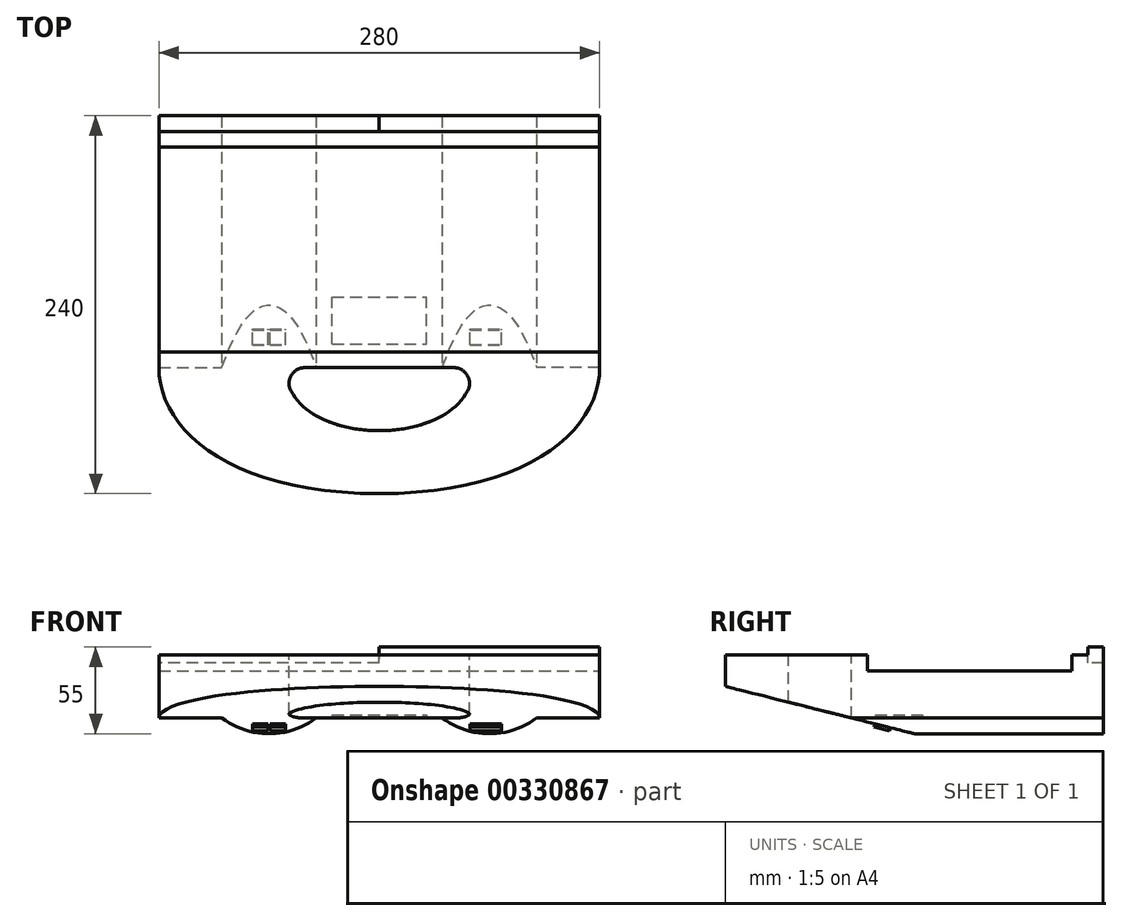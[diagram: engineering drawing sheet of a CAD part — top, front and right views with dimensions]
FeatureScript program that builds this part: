
annotation { "Feature Type Name" : "Feature", "Feature Type Description" : "" }
export const myFeature = defineFeature(function(context is Context, id is Id, definition is map)
    precondition{}
    {
        {
            var Q0;
            Q0=qCreatedBy(makeId("Front.planeOp"),FACE);
            var sketch = newSketch(context, id + "F0", { "sketchPlane" : qUnion([Q0])});
            skLineSegment(sketch, "E0", {"start": v(0, 34.56) * mm, "end": v(-140, 34.56) * mm});
            skLineSegment(sketch, "E1", {"start": v(-140, 34.56) * mm, "end": v(-140, -15.44) * mm});
            skLineSegment(sketch, "E2", {"start": v(-140, -15.44) * mm, "end": v(0, -15.44) * mm});
            skLineSegment(sketch, "E3.MirrorCS", {"start": v(0, 34.56) * mm, "end": v(140, 34.56) * mm});
            skLineSegment(sketch, "E4.MirrorCS", {"start": v(140, 34.56) * mm, "end": v(140, -15.44) * mm});
            skLineSegment(sketch, "E5.MirrorCS", {"start": v(140, -15.44) * mm, "end": v(0, -15.44) * mm});
            skSolve(sketch);
        }
        {
            var Q0;
            Q0 = qSketchRegion(id + "F0", true);
            extrude(context, id + "F1", {"entities" : qUnion([Q0]), "depth" : 240 * mm});
        }
        {
            var Q0;
            Q0=makeQuery(id+"F1.opExtrude","SWEPT_FACE",FACE,{"disambiguationData":[OSD([sQuery(id+"F0.wireOp",EDGE,"E0"),sQuery(id+"F0.wireOp",EDGE,"E3.MirrorCS")])]});
            var sketch = newSketch(context, id + "F2", { "sketchPlane" : qUnion([Q0])});
            skFitSpline(sketch, "E6", {"points": [v(0, -240) * mm, v(-140, -160) * mm], "startDerivative": vector(-286.06, 0) * mm, "endDerivative": vector(0, 116.3) * mm});
            skLineSegment(sketch, "E7", {"start": v(-140, -160) * mm, "end": v(-197.98, -160) * mm});
            skLineSegment(sketch, "E8", {"start": v(-197.98, -160) * mm, "end": v(-197.98, -279.95) * mm});
            skLineSegment(sketch, "E9", {"start": v(-197.98, -279.95) * mm, "end": v(0, -279.95) * mm});
            skLineSegment(sketch, "E10.MirrorCS", {"start": v(197.98, -279.95) * mm, "end": v(0, -279.95) * mm});
            skLineSegment(sketch, "E11.MirrorCS", {"start": v(197.98, -160) * mm, "end": v(197.98, -279.95) * mm});
            skLineSegment(sketch, "E12.MirrorCS", {"start": v(140, -160) * mm, "end": v(197.98, -160) * mm});
            skFitSpline(sketch, "E13.MirrorCS", {"points": [v(0, -240) * mm, v(140, -160) * mm], "startDerivative": vector(286.06, 0) * mm, "endDerivative": vector(0, 116.3) * mm});
            skSolve(sketch);
        }
        {
            var Q0;
            Q0=makeQuery(id+"F1.opExtrude","SWEPT_FACE",FACE,{"disambiguationData":[OSD([sQuery(id+"F0.wireOp",EDGE,"E4.MirrorCS")])]});
            var sketch = newSketch(context, id + "F3", { "sketchPlane" : qUnion([Q0])});
            skLineSegment(sketch, "E14", {"start": v(-240, 14.56) * mm, "end": v(-258.73, 14.56) * mm});
            skLineSegment(sketch, "E15", {"start": v(-258.73, 14.56) * mm, "end": v(-258.73, -38.28) * mm});
            skLineSegment(sketch, "E16", {"start": v(-258.73, -38.28) * mm, "end": v(-129.87, -38.28) * mm});
            skLineSegment(sketch, "E17", {"start": v(-129.87, -38.28) * mm, "end": v(-120, -15.44) * mm});
            skLineSegment(sketch, "E18", {"start": v(-240, 14.56) * mm, "end": v(-160, -5.44) * mm});
            skLineSegment(sketch, "E19", {"start": v(-160, -5.44) * mm, "end": v(-120, -15.44) * mm});
            skSolve(sketch);
        }
        {
            var Q0;
            Q0=makeQuery(id+"F1.opExtrude","CAP_FACE",FACE,{"disambiguationData":[OSD([sQuery(id+"F0.wireOp",EDGE,"E0"),sQuery(id+"F0.wireOp",EDGE,"E1"),sQuery(id+"F0.wireOp",EDGE,"E2"),sQuery(id+"F0.wireOp",EDGE,"E3.MirrorCS"),sQuery(id+"F0.wireOp",EDGE,"E4.MirrorCS"),sQuery(id+"F0.wireOp",EDGE,"E5.MirrorCS")])],"isStart":false});
            var sketch = newSketch(context, id + "F4", { "sketchPlane" : qUnion([Q0])});
            skLineSegment(sketch, "E20", {"start": v(-140, -5.44) * mm, "end": v(-165.94, -5.44) * mm});
            skLineSegment(sketch, "E21", {"start": v(-165.94, -5.44) * mm, "end": v(-165.94, -57.66) * mm});
            skLineSegment(sketch, "E22", {"start": v(-165.94, -57.66) * mm, "end": v(0, -57.66) * mm});
            skLineSegment(sketch, "E23", {"start": v(-140, -5.44) * mm, "end": v(-100, -5.44) * mm});
            skLineSegment(sketch, "E24", {"start": v(0, -5.44) * mm, "end": v(-40, -5.44) * mm});
            skArc(sketch, "E25", {"start": v(-70, -15.44) * mm, "mid": v(-85.81, -12.88) * mm, "end": v(-100, -5.44) * mm});
            skArc(sketch, "E26", {"start": v(-70, -15.44) * mm, "mid": v(-54.19, -12.88) * mm, "end": v(-40, -5.44) * mm});
            skLineSegment(sketch, "E27.MirrorCS", {"start": v(140, -5.44) * mm, "end": v(100, -5.44) * mm});
            skLineSegment(sketch, "E28.MirrorCS", {"start": v(140, -5.44) * mm, "end": v(165.94, -5.44) * mm});
            skLineSegment(sketch, "E29.MirrorCS", {"start": v(0, -5.44) * mm, "end": v(40, -5.44) * mm});
            skArc(sketch, "E30.MirrorCS", {"start": v(70, -15.44) * mm, "mid": v(85.81, -12.88) * mm, "end": v(100, -5.44) * mm});
            skLineSegment(sketch, "E31.MirrorCS", {"start": v(165.94, -57.66) * mm, "end": v(0, -57.66) * mm});
            skArc(sketch, "E32.MirrorCS", {"start": v(70, -15.44) * mm, "mid": v(54.19, -12.88) * mm, "end": v(40, -5.44) * mm});
            skLineSegment(sketch, "E33.MirrorCS", {"start": v(165.94, -5.44) * mm, "end": v(165.94, -57.66) * mm});
            skSolve(sketch);
        }
        {
            var Q0;
            Q0 = qSketchRegion(id + "F2", true);
            extrude(context, id + "F5", {"entities" : qUnion([Q0]), "operationType" : NewBodyOperationType.REMOVE, "oppositeDirection" : true, "depth" : 55 * mm});
        }
        {
            var Q0;
            Q0 = qSketchRegion(id + "F3", true);
            extrude(context, id + "F6", {"entities" : qUnion([Q0]), "operationType" : NewBodyOperationType.REMOVE, "oppositeDirection" : true, "depth" : 300 * mm});
        }
        {
            var Q0;
            Q0 = qSketchRegion(id + "F4", true);
            extrude(context, id + "F7", {"entities" : qUnion([Q0]), "operationType" : NewBodyOperationType.REMOVE, "oppositeDirection" : true, "depth" : 300 * mm});
        }
        {
            var Q0;
            Q0=makeQuery(id+"F1.opExtrude","SWEPT_FACE",FACE,{"disambiguationData":[OSD([sQuery(id+"F0.wireOp",EDGE,"E0"),sQuery(id+"F0.wireOp",EDGE,"E3.MirrorCS")])]});
            var sketch = newSketch(context, id + "F8", { "sketchPlane" : qUnion([Q0])});
            skLineSegment(sketch, "E34", {"start": v(-47.32, -160) * mm, "end": v(0, -160) * mm});
            skFitSpline(sketch, "E35", {"points": [v(-60, -160) * mm, v(0, -200.02) * mm], "startDerivative": vector(2.66, -80.66) * mm, "endDerivative": vector(88.67, 0) * mm});
            skFitSpline(sketch, "E36.MirrorCS", {"points": [v(60, -160) * mm, v(0, -200.02) * mm], "startDerivative": vector(-2.66, -80.66) * mm, "endDerivative": vector(-88.67, 0) * mm});
            skLineSegment(sketch, "E37.MirrorCS", {"start": v(47.32, -160) * mm, "end": v(0, -160) * mm});
            skArc(sketch, "E38.filletArc", {"start": v(-47.32, -160) * mm, "mid": v(-55.9, -164.85) * mm, "end": v(-56.14, -174.7) * mm});
            skArc(sketch, "E39.filletArc", {"start": v(56.14, -174.7) * mm, "mid": v(55.9, -164.85) * mm, "end": v(47.32, -160) * mm});
            skSolve(sketch);
        }
        {
            var Q0;
            Q0 = qSketchRegion(id + "F8", true);
            extrude(context, id + "F9", {"entities" : qUnion([Q0]), "operationType" : NewBodyOperationType.REMOVE, "oppositeDirection" : true, "depth" : 60 * mm});
        }
        {
            var Q0;
            Q0=makeQuery(id+"F1.opExtrude","SWEPT_FACE",FACE,{"disambiguationData":[OSD([sQuery(id+"F0.wireOp",EDGE,"E4.MirrorCS")])]});
            var sketch = newSketch(context, id + "F10", { "sketchPlane" : qUnion([Q0])});
            skLineSegment(sketch, "E40", {"start": v(-150, 34.56) * mm, "end": v(-150, 24.56) * mm});
            skLineSegment(sketch, "E41", {"start": v(-150, 24.56) * mm, "end": v(-20, 24.56) * mm});
            skLineSegment(sketch, "E42", {"start": v(-20, 24.56) * mm, "end": v(-20, 34.56) * mm});
            skLineSegment(sketch, "E43", {"start": v(-20, 34.56) * mm, "end": v(-20, 61.04) * mm});
            skLineSegment(sketch, "E44", {"start": v(-20, 61.04) * mm, "end": v(-150, 61.04) * mm});
            skLineSegment(sketch, "E45", {"start": v(-150, 61.04) * mm, "end": v(-150, 34.56) * mm});
            skSolve(sketch);
        }
        {
            var Q0;
            Q0 = qSketchRegion(id + "F10", true);
            extrude(context, id + "F11", {"entities" : qUnion([Q0]), "operationType" : NewBodyOperationType.REMOVE, "oppositeDirection" : true, "depth" : 300 * mm});
        }
        {
            var Q0;
            Q0=makeQuery(id+"F1.opExtrude","SWEPT_FACE",FACE,{"disambiguationData":[OSD([sQuery(id+"F0.wireOp",EDGE,"E1")])]});
            var sketch = newSketch(context, id + "F12", { "sketchPlane" : qUnion([Q0])});
            skLineSegment(sketch, "E46", {"start": v(0, 34.56) * mm, "end": v(0, 24.56) * mm});
            skLineSegment(sketch, "E47", {"start": v(0, 24.56) * mm, "end": v(10, 24.56) * mm});
            skLineSegment(sketch, "E48", {"start": v(10, 24.56) * mm, "end": v(10, 34.56) * mm});
            skLineSegment(sketch, "E49", {"start": v(10, 34.56) * mm, "end": v(0, 34.56) * mm});
            skSolve(sketch);
        }
        {
            var Q0;
            Q0 = qSketchRegion(id + "F12", true);
            extrude(context, id + "F13", {"entities" : qUnion([Q0]), "operationType" : NewBodyOperationType.REMOVE, "oppositeDirection" : true, "depth" : 140 * mm});
        }
        {
            var Q0;
            Q0=makeQuery(id+"F1.opExtrude","SWEPT_FACE",FACE,{"disambiguationData":[OSD([sQuery(id+"F0.wireOp",EDGE,"E4.MirrorCS")])]});
            var sketch = newSketch(context, id + "F14", { "sketchPlane" : qUnion([Q0])});
            skLineSegment(sketch, "E50", {"start": v(0, 34.56) * mm, "end": v(0, 39.56) * mm});
            skLineSegment(sketch, "E51", {"start": v(0, 39.56) * mm, "end": v(-10, 39.56) * mm});
            skLineSegment(sketch, "E52", {"start": v(-10, 39.56) * mm, "end": v(-10, 34.56) * mm});
            skSolve(sketch);
        }
        {
            var Q0;
            {var subQ0=sQuery(id+"F14.wireOp",EDGE,"E50");Q0=makeQuery(id+"F14.imprint","IMPRINT",FACE,{"disambiguationData":[TD([[makeQuery(id+"F14.imprint","IMPRINT",EDGE,{"derivedFrom":subQ0}),1.0]])]});}
            extrude(context, id + "F15", {"entities" : qUnion([Q0]), "operationType" : NewBodyOperationType.ADD, "oppositeDirection" : true, "depth" : 140 * mm});
        }
        {
            var Q0;
            Q0=makeQuery(id+"F1.opExtrude","SWEPT_FACE",FACE,{"disambiguationData":[OSD([sQuery(id+"F0.wireOp",EDGE,"E1")])]});
            var sketch = newSketch(context, id + "F16", { "sketchPlane" : qUnion([Q0])});
            skLineSegment(sketch, "E53", {"start": v(0, 24.56) * mm, "end": v(0, 29.56) * mm});
            skLineSegment(sketch, "E54", {"start": v(0, 29.56) * mm, "end": v(10, 29.56) * mm});
            skLineSegment(sketch, "E55", {"start": v(10, 29.56) * mm, "end": v(10, 24.56) * mm});
            skSolve(sketch);
        }
        {
            var Q0;
            Q0=makeQuery(id+"F16.imprint","IMPRINT",FACE,{"disambiguationData":[TD([[makeQuery(id+"F16.imprint","IMPRINT",EDGE,{"derivedFrom":sQuery(id+"F16.wireOp",EDGE,"E53")}),-1.0]])]});
            extrude(context, id + "F17", {"entities" : qUnion([Q0]), "operationType" : NewBodyOperationType.ADD, "oppositeDirection" : true, "depth" : 140 * mm});
        }
        {
            var Q0;
            Q0=makeQuery(id+"F7.boolean.opBoolean","COPY",FACE,{"derivedFrom":makeQuery(id+"F7.opExtrude","SWEPT_FACE",FACE,{"disambiguationData":[OSD([sQuery(id+"F4.wireOp",EDGE,"E24"),sQuery(id+"F4.wireOp",EDGE,"E29.MirrorCS")])]})});
            var sketch = newSketch(context, id + "F18", { "sketchPlane" : qUnion([Q0])});
            skLineSegment(sketch, "E56.bottom", {"start": v(-30, 145) * mm, "end": v(30, 145) * mm});
            skLineSegment(sketch, "E56.top", {"start": v(-30, 115) * mm, "end": v(30, 115) * mm});
            skLineSegment(sketch, "E56.left", {"start": v(-30, 145) * mm, "end": v(-30, 115) * mm});
            skLineSegment(sketch, "E56.right", {"start": v(30, 145) * mm, "end": v(30, 115) * mm});
            skSolve(sketch);
        }
        {
            var Q0;
            Q0=makeQuery(id+"F18.imprint","IMPRINT",FACE,{"disambiguationData":[TD([[makeQuery(id+"F18.imprint","IMPRINT",EDGE,{"derivedFrom":sQuery(id+"F18.wireOp",EDGE,"E56.bottom")}),-1.0]])]});
            extrude(context, id + "F19", {"entities" : qUnion([Q0]), "operationType" : NewBodyOperationType.REMOVE, "oppositeDirection" : true, "depth" : 2 * mm});
        }
        {
            var Q0;
            Q0=makeQuery(id+"F6.boolean.opBoolean","COPY",FACE,{"derivedFrom":makeQuery(id+"F6.opExtrude","SWEPT_FACE",FACE,{"disambiguationData":[OSD([sQuery(id+"F3.wireOp",EDGE,"E18"),sQuery(id+"F3.wireOp",EDGE,"E19")])]})});
            var sketch = newSketch(context, id + "F20", { "sketchPlane" : qUnion([Q0])});
            skLineSegment(sketch, "E57.bottom", {"start": v(-80.5, 138.63) * mm, "end": v(-70.5, 138.63) * mm});
            skLineSegment(sketch, "E57.top", {"start": v(-80.5, 128.63) * mm, "end": v(-70.5, 128.63) * mm});
            skLineSegment(sketch, "E57.left", {"start": v(-80.5, 138.63) * mm, "end": v(-80.5, 128.63) * mm});
            skLineSegment(sketch, "E57.right", {"start": v(-70.5, 138.63) * mm, "end": v(-70.5, 128.63) * mm});
            skLineSegment(sketch, "E58.bottom", {"start": v(-69.5, 138.63) * mm, "end": v(-59.5, 138.63) * mm});
            skLineSegment(sketch, "E58.top", {"start": v(-69.5, 128.63) * mm, "end": v(-59.5, 128.63) * mm});
            skLineSegment(sketch, "E58.left", {"start": v(-69.5, 138.63) * mm, "end": v(-69.5, 128.63) * mm});
            skLineSegment(sketch, "E58.right", {"start": v(-59.5, 138.63) * mm, "end": v(-59.5, 128.63) * mm});
            skPoint(sketch, "E59.firstSnap0", {"position": v(-75.5, 138.63) * mm});
            skLineSegment(sketch, "E59.bottom", {"start": v(57.5, 138.63) * mm, "end": v(77.5, 138.63) * mm});
            skLineSegment(sketch, "E59.top", {"start": v(57.5, 128.63) * mm, "end": v(77.5, 128.63) * mm});
            skLineSegment(sketch, "E59.left", {"start": v(57.5, 138.63) * mm, "end": v(57.5, 128.63) * mm});
            skLineSegment(sketch, "E59.right", {"start": v(77.5, 138.63) * mm, "end": v(77.5, 128.63) * mm});
            skSolve(sketch);
        }
        {
            var Q0;
            Q0 = qSketchRegion(id + "F20", true);
            extrude(context, id + "F21", {"entities" : qUnion([Q0]), "operationType" : NewBodyOperationType.ADD, "depth" : 2 * mm});
        }
    });
